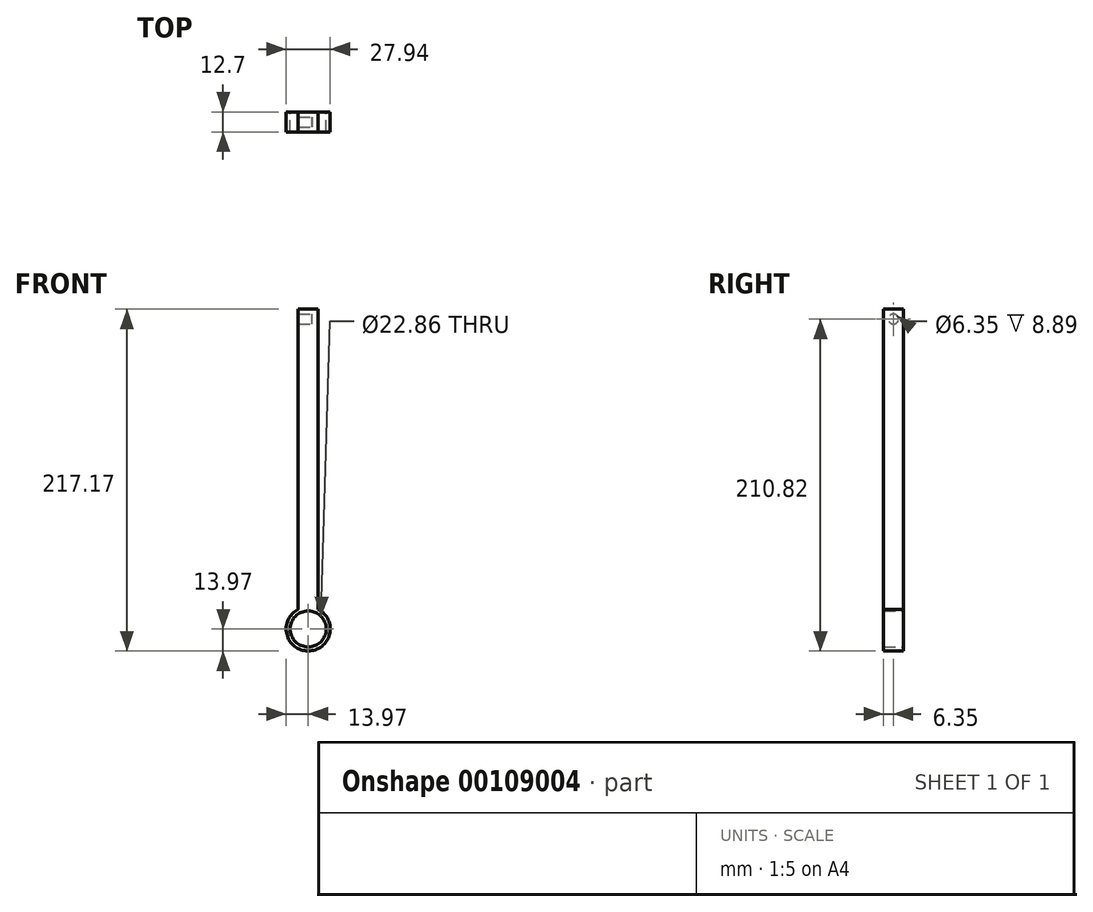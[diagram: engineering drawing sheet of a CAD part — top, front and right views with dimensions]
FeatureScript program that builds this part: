
annotation { "Feature Type Name" : "Feature", "Feature Type Description" : "" }
export const myFeature = defineFeature(function(context is Context, id is Id, definition is map)
    precondition{}
    {
        {
            var Q0;
            Q0=qCreatedBy(makeId("Front.planeOp"),FACE);
            var sketch = newSketch(context, id + "F0", { "sketchPlane" : qUnion([Q0])});
            skCircle(sketch, "E0", {"center": v(0, 0) * mm, "radius": 11.43 * mm});
            skCircle(sketch, "E1", {"center": v(0, 0) * mm, "radius": 13.97 * mm});
            skSolve(sketch);
        }
        {
            var Q0;
            Q0=makeQuery(id+"F0.imprint","IMPRINT",FACE,{"disambiguationData":[TD([[makeQuery(id+"F0.imprint","IMPRINT",EDGE,{"derivedFrom":sQuery(id+"F0.wireOp",EDGE,"E0")}),-1.0]])]});
            extrude(context, id + "F1", {"entities" : qUnion([Q0]), "depth" : 12.7 * mm});
        }
        {
            var Q0;
            Q0=qCreatedBy(makeId("Right.planeOp"),FACE);
            var sketch = newSketch(context, id + "F2", { "sketchPlane" : qUnion([Q0])});
            skLineSegment(sketch, "E2", {"start": v(0, 0) * mm, "end": v(-12.7, 0) * mm});
            skLineSegment(sketch, "E3", {"start": v(0, 0) * mm, "end": v(0, 203.2) * mm});
            skLineSegment(sketch, "E4", {"start": v(0, 203.2) * mm, "end": v(-12.7, 203.2) * mm});
            skLineSegment(sketch, "E5", {"start": v(-12.7, 203.2) * mm, "end": v(-12.7, 0) * mm});
            skSolve(sketch);
        }
        {
            var Q0;
            Q0=makeQuery(id+"F2.imprint","IMPRINT",FACE,{"disambiguationData":[TD([[makeQuery(id+"F2.imprint","IMPRINT",EDGE,{"derivedFrom":sQuery(id+"F2.wireOp",EDGE,"E2")}),-1.0]])]});
            extrude(context, id + "F3", {"entities" : qUnion([Q0]), "operationType" : NewBodyOperationType.ADD, "depth" : 6.35 * mm, "hasSecondDirection" : true, "secondDirectionOppositeDirection" : true, "secondDirectionDepth" : 6.35 * mm});
        }
        {
            var Q0;
            Q0=makeQuery(id+"F0.imprint","IMPRINT",FACE,{"disambiguationData":[TD([[makeQuery(id+"F0.imprint","IMPRINT",EDGE,{"derivedFrom":sQuery(id+"F0.wireOp",EDGE,"E0")}),1.0]])]});
            extrude(context, id + "F4", {"entities" : qUnion([Q0]), "operationType" : NewBodyOperationType.REMOVE, "depth" : 25.4 * mm});
        }
        {
            var Q0;
            {var subQ0=sQuery(id+"F0.wireOp",EDGE,"E1");var subQ2=sQuery(id+"F2.wireOp",EDGE,"E3");var subQ3=sQuery(id+"F2.wireOp",EDGE,"E5");var subQ4=sQuery(id+"F2.wireOp",EDGE,"E4");Q0=makeQuery(id+"F3.boolean.opBoolean","SPLIT",FACE,{"disambiguationData":[TD([makeQuery(id+"F1.opExtrude","SWEPT_FACE",FACE,{"disambiguationData":[OSD([subQ0])]})])],"derivedFrom":makeQuery(id+"F3.opExtrude","CAP_FACE",FACE,{"disambiguationData":[OSD([sQuery(id+"F2.wireOp",EDGE,"E2"),subQ2,subQ4,subQ3])],"isStart":false})});}
            var sketch = newSketch(context, id + "F5", { "sketchPlane" : qUnion([Q0])});
            skLineSegment(sketch, "E6", {"start": v(-6.35, 203.2) * mm, "end": v(-6.35, 196.85) * mm});
            skCircle(sketch, "E7", {"center": v(-6.35, 196.85) * mm, "radius": 3.18 * mm});
            skSolve(sketch);
        }
        {
            var Q0;
            Q0=makeQuery(id+"F5.imprint","IMPRINT",FACE,{"disambiguationData":[TD([[makeQuery(id+"F5.imprint","IMPRINT",EDGE,{"derivedFrom":sQuery(id+"F5.wireOp",EDGE,"E7")}),1.0]])]});
            extrude(context, id + "F6", {"entities" : qUnion([Q0]), "operationType" : NewBodyOperationType.REMOVE, "oppositeDirection" : true, "depth" : 14.36 * mm, "hasSecondDirection" : true, "secondDirectionOppositeDirection" : true, "secondDirectionDepth" : 3.8 * mm});
        }
    });
